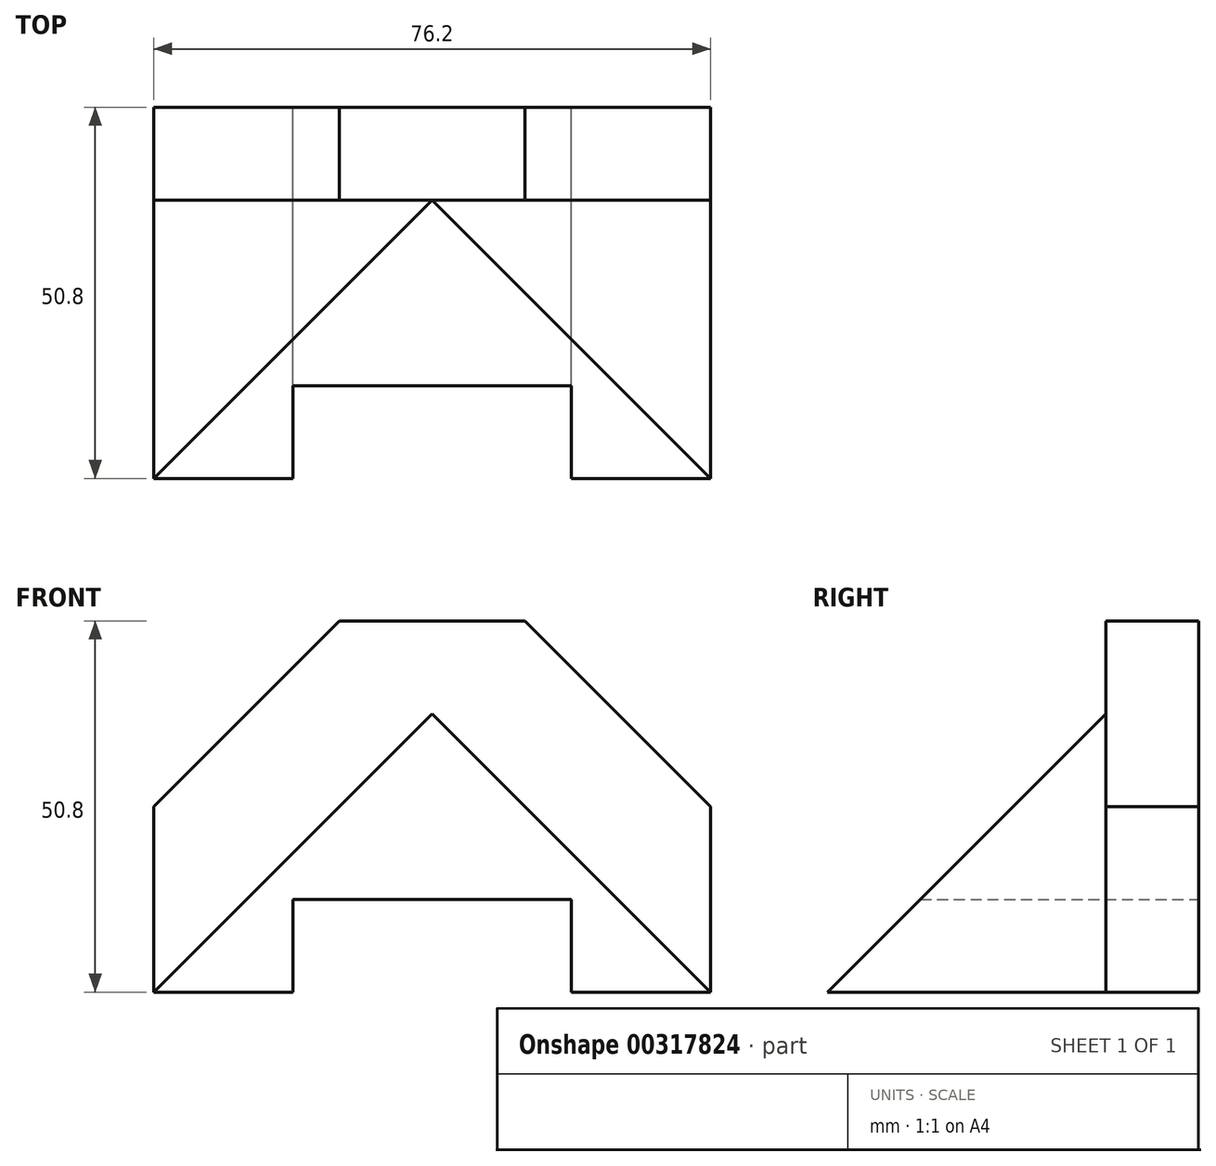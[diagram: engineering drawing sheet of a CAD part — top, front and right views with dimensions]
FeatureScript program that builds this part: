
annotation { "Feature Type Name" : "Feature", "Feature Type Description" : "" }
export const myFeature = defineFeature(function(context is Context, id is Id, definition is map)
    precondition{}
    {
        {
            var Q0;
            Q0=qCreatedBy(makeId("Front.planeOp"),FACE);
            var sketch = newSketch(context, id + "F0", { "sketchPlane" : qUnion([Q0])});
            skLineSegment(sketch, "E0", {"start": v(0, 0) * mm, "end": v(76.2, 0) * mm});
            skLineSegment(sketch, "E1", {"start": v(0, 0) * mm, "end": v(38.1, 38.1) * mm});
            skLineSegment(sketch, "E2", {"start": v(38.1, 38.1) * mm, "end": v(76.2, 0) * mm});
            skLineSegment(sketch, "E3", {"start": v(76.2, 0) * mm, "end": v(76.2, 25.4) * mm});
            skLineSegment(sketch, "E4", {"start": v(0, 25.4) * mm, "end": v(0, 0) * mm});
            skLineSegment(sketch, "E5", {"start": v(76.2, 25.4) * mm, "end": v(50.8, 50.8) * mm});
            skLineSegment(sketch, "E6", {"start": v(50.8, 50.8) * mm, "end": v(25.4, 50.8) * mm});
            skLineSegment(sketch, "E7", {"start": v(25.4, 50.8) * mm, "end": v(0, 25.4) * mm});
            skLineSegment(sketch, "E8", {"start": v(19.05, 0) * mm, "end": v(19.05, 12.7) * mm});
            skLineSegment(sketch, "E9", {"start": v(19.05, 12.7) * mm, "end": v(57.15, 12.7) * mm});
            skLineSegment(sketch, "E10", {"start": v(57.15, 12.7) * mm, "end": v(57.15, 0) * mm});
            skSolve(sketch);
        }
        {
            var Q0;
            {var subQ1=sQuery(id+"F0.wireOp",EDGE,"E1");Q0=makeQuery(id+"F0.imprint","IMPRINT",FACE,{"disambiguationData":[TD([[makeQuery(id+"F0.imprint","IMPRINT",EDGE,{"derivedFrom":subQ1}),-1.0]])]});}
            extrude(context, id + "F1", {"entities" : qUnion([Q0]), "depth" : 50.8 * mm});
        }
        {
            var Q0;
            Q0=makeQuery(id+"F0.imprint","IMPRINT",FACE,{"disambiguationData":[TD([[makeQuery(id+"F0.imprint","IMPRINT",EDGE,{"derivedFrom":sQuery(id+"F0.wireOp",EDGE,"E1")}),1.0]])]});
            extrude(context, id + "F2", {"entities" : qUnion([Q0]), "operationType" : NewBodyOperationType.ADD, "depth" : 12.7 * mm});
        }
        {
            var Q0;
            Q0=qCreatedBy(makeId("Right.planeOp"),FACE);
            var sketch = newSketch(context, id + "F3", { "sketchPlane" : qUnion([Q0])});
            skLineSegment(sketch, "E11", {"start": v(-12.7, 0) * mm, "end": v(-50.8, 0) * mm});
            skLineSegment(sketch, "E12", {"start": v(-50.8, 0) * mm, "end": v(-50.8, 38.1) * mm});
            skLineSegment(sketch, "E13", {"start": v(-50.8, 38.1) * mm, "end": v(-12.7, 38.1) * mm});
            skLineSegment(sketch, "E14", {"start": v(-12.7, 38.1) * mm, "end": v(-50.8, 0) * mm});
            skSolve(sketch);
        }
        {
            var Q0;
            Q0=makeQuery(id+"F3.imprint","IMPRINT",FACE,{"disambiguationData":[TD([[makeQuery(id+"F3.imprint","IMPRINT",EDGE,{"derivedFrom":sQuery(id+"F3.wireOp",EDGE,"E12")}),-1.0]])]});
            extrude(context, id + "F4", {"entities" : qUnion([Q0]), "operationType" : NewBodyOperationType.REMOVE, "endBound" : BoundingType.THROUGH_ALL, "depth" : 50.8 * mm});
        }
    });
